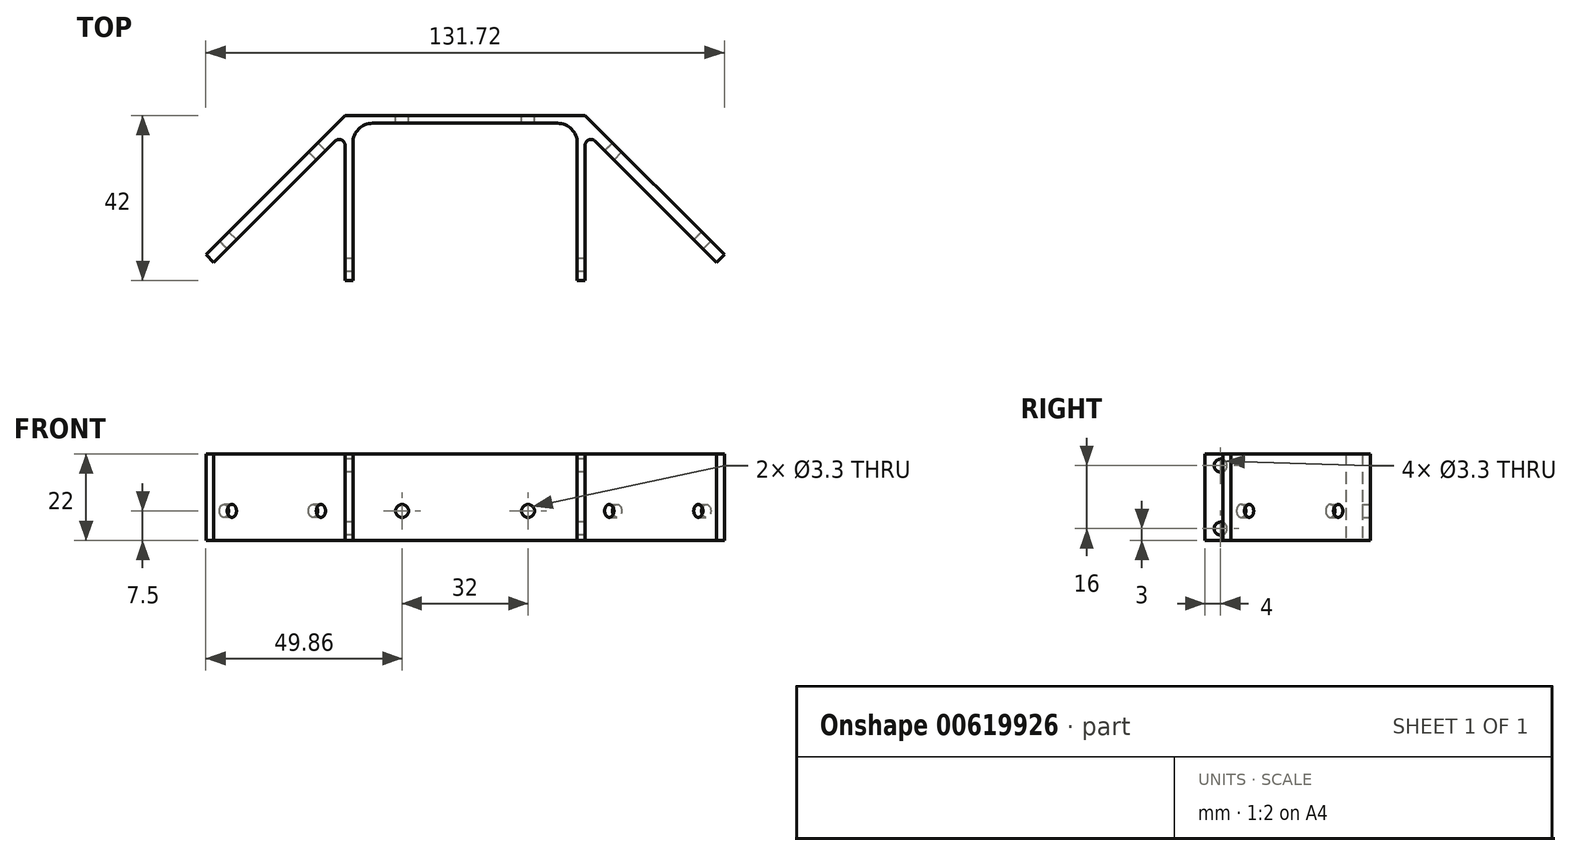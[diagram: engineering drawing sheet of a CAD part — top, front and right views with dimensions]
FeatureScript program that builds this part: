
annotation { "Feature Type Name" : "Feature", "Feature Type Description" : "" }
export const myFeature = defineFeature(function(context is Context, id is Id, definition is map)
    precondition{}
    {
        {
            var Q0;
            Q0=qCreatedBy(makeId("Top.planeOp"),FACE);
            var sketch = newSketch(context, id + "F0", { "sketchPlane" : qUnion([Q0])});
            skLineSegment(sketch, "E0.bottom", {"start": v(-28.5, 20) * mm, "end": v(28.5, 20) * mm});
            skLineSegment(sketch, "E0.left", {"start": v(-28.5, 20) * mm, "end": v(-28.5, -20) * mm});
            skLineSegment(sketch, "E0.right", {"start": v(28.5, 20) * mm, "end": v(28.5, -20) * mm});
            skLineSegment(sketch, "E1.bottom", {"start": v(-30.5, 22) * mm, "end": v(30.5, 22) * mm});
            skLineSegment(sketch, "E1.top", {"start": v(-30.5, -20) * mm, "end": v(-28.5, -20) * mm});
            skLineSegment(sketch, "E1.left", {"start": v(-30.5, 18) * mm, "end": v(-30.5, -20) * mm});
            skLineSegment(sketch, "E1.right", {"start": v(30.5, 18) * mm, "end": v(30.5, -20) * mm});
            skLineSegment(sketch, "E2", {"start": v(-30.5, 22) * mm, "end": v(-65.86, -13.36) * mm});
            skLineSegment(sketch, "E3", {"start": v(-30.5, 18) * mm, "end": v(-63.86, -15.36) * mm});
            skLineSegment(sketch, "E4", {"start": v(30.5, 22) * mm, "end": v(65.86, -13.36) * mm});
            skLineSegment(sketch, "E5", {"start": v(30.5, 18) * mm, "end": v(63.86, -15.36) * mm});
            skLineSegment(sketch, "E6", {"start": v(-65.86, -13.36) * mm, "end": v(-63.86, -15.36) * mm});
            skLineSegment(sketch, "E7", {"start": v(65.86, -13.36) * mm, "end": v(63.86, -15.36) * mm});
            skLineSegment(sketch, "E8.trimOffspring", {"start": v(28.5, -20) * mm, "end": v(30.5, -20) * mm});
            skSolve(sketch);
        }
        {
            var Q0;
            Q0=makeQuery(id+"F0.imprint","IMPRINT",FACE,{"disambiguationData":[TD([[makeQuery(id+"F0.imprint","IMPRINT",EDGE,{"derivedFrom":sQuery(id+"F0.wireOp",EDGE,"E0.bottom")}),1.0]])]});
            extrude(context, id + "F1", {"entities" : qUnion([Q0]), "depth" : 22 * mm, "offsetDistance" : 25 * mm});
        }
        {
            var Q0;
            Q0=makeQuery(id+"F1.opExtrude","SWEPT_FACE",FACE,{"disambiguationData":[OSD([sQuery(id+"F0.wireOp",EDGE,"E4")])]});
            var sketch = newSketch(context, id + "F2", { "sketchPlane" : qUnion([Q0])});
            skPoint(sketch, "E9", {"position": v(-17.51, 7.5) * mm});
            skPoint(sketch, "E10", {"position": v(-49.51, 7.5) * mm});
            skSolve(sketch);
        }
        {
            var Q0;
            Q0=sQuery(id+"F2.wireOp",VERTEX,"E9");
            var Q1;
            Q1=sQuery(id+"F2.wireOp",VERTEX,"E10");
            var Q2;
            Q2=makeQuery(id+"F1.opExtrude","SWEPT_BODY",BODY,{"disambiguationData":[OSD([sQuery(id+"F0.wireOp",EDGE,"E0.bottom"),sQuery(id+"F0.wireOp",EDGE,"E0.left"),sQuery(id+"F0.wireOp",EDGE,"E0.right"),sQuery(id+"F0.wireOp",EDGE,"E1.bottom"),sQuery(id+"F0.wireOp",EDGE,"E1.top"),sQuery(id+"F0.wireOp",EDGE,"E1.left"),sQuery(id+"F0.wireOp",EDGE,"E1.right"),sQuery(id+"F0.wireOp",EDGE,"E2"),sQuery(id+"F0.wireOp",EDGE,"E3"),sQuery(id+"F0.wireOp",EDGE,"E4"),sQuery(id+"F0.wireOp",EDGE,"E5"),sQuery(id+"F0.wireOp",EDGE,"E6"),sQuery(id+"F0.wireOp",EDGE,"E7"),sQuery(id+"F0.wireOp",EDGE,"E8.trimOffspring")])]});
            hole(context, id + "F3", {"style" : HoleStyle.SIMPLE, "endStyle" : HoleEndStyle.BLIND, "standardTappedOrClearance" : lookupTablePath({ "standard" : "ISO", "fit" : "Normal", "size" : "M3", "type" : "Clearance" }), "standardBlindInLast" : lookupTablePath({ "fit" : "Standard", "standard" : "ISO", "size" : "M3", "type" : "Clearance" }), "holeDiameter" : 3.3 * mm, "majorDiameter" : 3 * mm, "holeDepth" : 3 * mm, "isTappedThrough" : true, "tappedDepth" : 12 * mm, "tapClearance" : 3, "locations" : qUnion([Q0, Q1]), "scope" : qUnion([Q2])});
        }
        {
            var Q0;
            Q0=makeQuery(id+"F1.opExtrude","SWEPT_EDGE",EDGE,{"disambiguationData":[OSD([sQuery(id+"F0.wireOp",EDGE,"E1.left"),sQuery(id+"F0.wireOp",EDGE,"E3")])]});
            var Q1;
            Q1=makeQuery(id+"F1.opExtrude","SWEPT_EDGE",EDGE,{"disambiguationData":[OSD([sQuery(id+"F0.wireOp",EDGE,"E1.right"),sQuery(id+"F0.wireOp",EDGE,"E5")])]});
            fillet(context, id + "F4", {"entities" : qUnion([Q0, Q1]), "radius" : 1.5 * mm, "tangentPropagation" : true, "allowEdgeOverflow" : false});
        }
        {
            var Q0;
            Q0=makeQuery(id+"F1.opExtrude","SWEPT_EDGE",EDGE,{"disambiguationData":[OSD([sQuery(id+"F0.wireOp",EDGE,"E0.bottom"),sQuery(id+"F0.wireOp",EDGE,"E0.left")])]});
            var Q1;
            Q1=makeQuery(id+"F1.opExtrude","SWEPT_EDGE",EDGE,{"disambiguationData":[OSD([sQuery(id+"F0.wireOp",EDGE,"E0.bottom"),sQuery(id+"F0.wireOp",EDGE,"E0.right")])]});
            fillet(context, id + "F5", {"entities" : qUnion([Q0, Q1]), "radius" : 5 * mm, "tangentPropagation" : true, "allowEdgeOverflow" : false});
        }
        {
            var Q0;
            Q0=makeQuery(id+"F1.opExtrude","SWEPT_FACE",FACE,{"disambiguationData":[OSD([sQuery(id+"F0.wireOp",EDGE,"E2")])]});
            var sketch = newSketch(context, id + "F6", { "sketchPlane" : qUnion([Q0])});
            skPoint(sketch, "E11", {"position": v(17.51, 7.5) * mm});
            skPoint(sketch, "E12", {"position": v(49.51, 7.5) * mm});
            skSolve(sketch);
        }
        {
            var Q0;
            Q0=sQuery(id+"F6.wireOp",VERTEX,"E11");
            var Q1;
            Q1=sQuery(id+"F6.wireOp",VERTEX,"E12");
            var Q2;
            Q2=makeQuery(id+"F1.opExtrude","SWEPT_BODY",BODY,{"disambiguationData":[OSD([sQuery(id+"F0.wireOp",EDGE,"E0.bottom"),sQuery(id+"F0.wireOp",EDGE,"E0.left"),sQuery(id+"F0.wireOp",EDGE,"E0.right"),sQuery(id+"F0.wireOp",EDGE,"E1.bottom"),sQuery(id+"F0.wireOp",EDGE,"E1.top"),sQuery(id+"F0.wireOp",EDGE,"E1.left"),sQuery(id+"F0.wireOp",EDGE,"E1.right"),sQuery(id+"F0.wireOp",EDGE,"E2"),sQuery(id+"F0.wireOp",EDGE,"E3"),sQuery(id+"F0.wireOp",EDGE,"E4"),sQuery(id+"F0.wireOp",EDGE,"E5"),sQuery(id+"F0.wireOp",EDGE,"E6"),sQuery(id+"F0.wireOp",EDGE,"E7"),sQuery(id+"F0.wireOp",EDGE,"E8.trimOffspring")])]});
            hole(context, id + "F7", {"style" : HoleStyle.SIMPLE, "endStyle" : HoleEndStyle.BLIND, "standardTappedOrClearance" : lookupTablePath({ "standard" : "ISO", "fit" : "Normal", "size" : "M3", "type" : "Clearance" }), "standardBlindInLast" : lookupTablePath({ "fit" : "Standard", "standard" : "ISO", "size" : "M3", "type" : "Clearance" }), "holeDiameter" : 3.3 * mm, "majorDiameter" : 5 * mm, "holeDepth" : 3 * mm, "isTappedThrough" : true, "tappedDepth" : 12 * mm, "tapClearance" : 3, "locations" : qUnion([Q0, Q1]), "scope" : qUnion([Q2])});
        }
        {
            var Q0;
            Q0=makeQuery(id+"F1.opExtrude","SWEPT_FACE",FACE,{"disambiguationData":[OSD([sQuery(id+"F0.wireOp",EDGE,"E1.bottom")])]});
            var sketch = newSketch(context, id + "F8", { "sketchPlane" : qUnion([Q0])});
            skPoint(sketch, "E13", {"position": v(-16, 7.5) * mm});
            skPoint(sketch, "E14", {"position": v(16, 7.5) * mm});
            skSolve(sketch);
        }
        {
            var Q0;
            Q0=sQuery(id+"F8.wireOp",VERTEX,"E13");
            var Q1;
            Q1=sQuery(id+"F8.wireOp",VERTEX,"E14");
            var Q2;
            Q2=makeQuery(id+"F1.opExtrude","SWEPT_BODY",BODY,{"disambiguationData":[OSD([sQuery(id+"F0.wireOp",EDGE,"E0.bottom"),sQuery(id+"F0.wireOp",EDGE,"E0.left"),sQuery(id+"F0.wireOp",EDGE,"E0.right"),sQuery(id+"F0.wireOp",EDGE,"E1.bottom"),sQuery(id+"F0.wireOp",EDGE,"E1.top"),sQuery(id+"F0.wireOp",EDGE,"E1.left"),sQuery(id+"F0.wireOp",EDGE,"E1.right"),sQuery(id+"F0.wireOp",EDGE,"E2"),sQuery(id+"F0.wireOp",EDGE,"E3"),sQuery(id+"F0.wireOp",EDGE,"E4"),sQuery(id+"F0.wireOp",EDGE,"E5"),sQuery(id+"F0.wireOp",EDGE,"E6"),sQuery(id+"F0.wireOp",EDGE,"E7"),sQuery(id+"F0.wireOp",EDGE,"E8.trimOffspring")])]});
            hole(context, id + "F9", {"style" : HoleStyle.SIMPLE, "endStyle" : HoleEndStyle.BLIND, "standardTappedOrClearance" : lookupTablePath({ "standard" : "ISO", "fit" : "Normal", "size" : "M3", "type" : "Clearance" }), "standardBlindInLast" : lookupTablePath({ "fit" : "Standard", "standard" : "ISO", "size" : "M3", "type" : "Clearance" }), "holeDiameter" : 3.3 * mm, "majorDiameter" : 5 * mm, "holeDepth" : 3 * mm, "isTappedThrough" : true, "tappedDepth" : 12 * mm, "tapClearance" : 3, "locations" : qUnion([Q0, Q1]), "scope" : qUnion([Q2])});
        }
        {
            var Q0;
            Q0=makeQuery(id+"F1.opExtrude","SWEPT_FACE",FACE,{"disambiguationData":[OSD([sQuery(id+"F0.wireOp",EDGE,"E1.left")])]});
            var sketch = newSketch(context, id + "F10", { "sketchPlane" : qUnion([Q0])});
            skPoint(sketch, "E15", {"position": v(16, 19) * mm});
            skPoint(sketch, "E16", {"position": v(16, 3) * mm});
            skSolve(sketch);
        }
        {
            var Q0;
            Q0=sQuery(id+"F10.wireOp",VERTEX,"E15");
            var Q1;
            Q1=sQuery(id+"F10.wireOp",VERTEX,"E16");
            var Q2;
            Q2=makeQuery(id+"F1.opExtrude","SWEPT_BODY",BODY,{"disambiguationData":[OSD([sQuery(id+"F0.wireOp",EDGE,"E0.bottom"),sQuery(id+"F0.wireOp",EDGE,"E0.left"),sQuery(id+"F0.wireOp",EDGE,"E0.right"),sQuery(id+"F0.wireOp",EDGE,"E1.bottom"),sQuery(id+"F0.wireOp",EDGE,"E1.top"),sQuery(id+"F0.wireOp",EDGE,"E1.left"),sQuery(id+"F0.wireOp",EDGE,"E1.right"),sQuery(id+"F0.wireOp",EDGE,"E2"),sQuery(id+"F0.wireOp",EDGE,"E3"),sQuery(id+"F0.wireOp",EDGE,"E4"),sQuery(id+"F0.wireOp",EDGE,"E5"),sQuery(id+"F0.wireOp",EDGE,"E6"),sQuery(id+"F0.wireOp",EDGE,"E7"),sQuery(id+"F0.wireOp",EDGE,"E8.trimOffspring")])]});
            hole(context, id + "F11", {"style" : HoleStyle.SIMPLE, "endStyle" : HoleEndStyle.BLIND, "standardTappedOrClearance" : lookupTablePath({ "standard" : "ISO", "fit" : "Normal", "size" : "M3", "type" : "Clearance" }), "standardBlindInLast" : lookupTablePath({ "fit" : "Standard", "standard" : "ISO", "size" : "M3", "type" : "Clearance" }), "holeDiameter" : 3.3 * mm, "majorDiameter" : 3 * mm, "holeDepth" : 63 * mm, "isTappedThrough" : true, "tappedDepth" : 12 * mm, "tapClearance" : 3, "locations" : qUnion([Q0, Q1]), "scope" : qUnion([Q2])});
        }
    });
